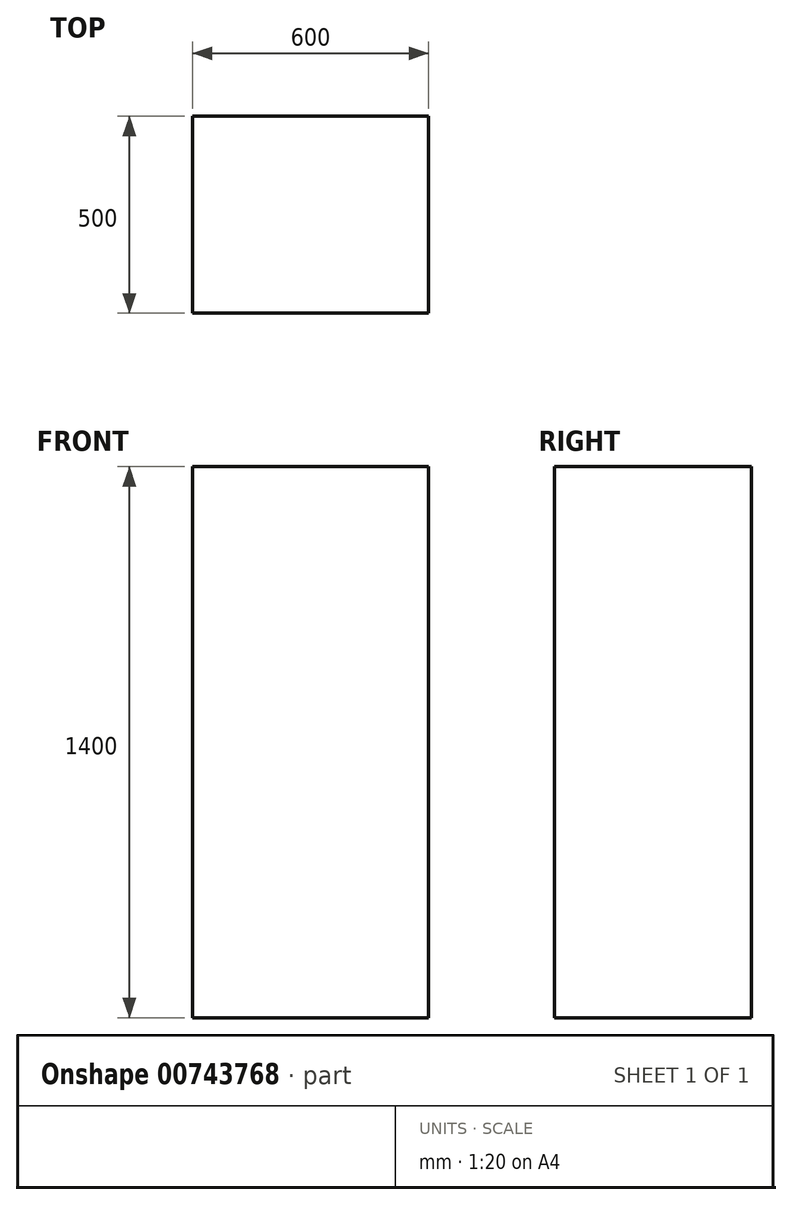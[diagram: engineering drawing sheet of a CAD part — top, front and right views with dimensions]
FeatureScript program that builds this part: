
annotation { "Feature Type Name" : "Feature", "Feature Type Description" : "" }
export const myFeature = defineFeature(function(context is Context, id is Id, definition is map)
    precondition{}
    {
        {
            var Q0;
            Q0=qCreatedBy(makeId("Front.planeOp"),FACE);
            var sketch = newSketch(context, id + "F0", { "sketchPlane" : qUnion([Q0])});
            skLineSegment(sketch, "E0.bottom", {"start": v(-428.4, 690.26) * mm, "end": v(171.6, 690.26) * mm});
            skLineSegment(sketch, "E0.top", {"start": v(-428.4, -709.74) * mm, "end": v(171.6, -709.74) * mm});
            skLineSegment(sketch, "E0.left", {"start": v(-428.4, 690.26) * mm, "end": v(-428.4, -709.74) * mm});
            skLineSegment(sketch, "E0.right", {"start": v(171.6, 690.26) * mm, "end": v(171.6, -709.74) * mm});
            skSolve(sketch);
        }
        {
            var Q0;
            Q0 = qSketchRegion(id + "F0", true);
            extrude(context, id + "F1", {"entities" : qUnion([Q0]), "oppositeDirection" : true, "depth" : 500 * mm, "offsetDistance" : 25 * mm});
        }
    });
